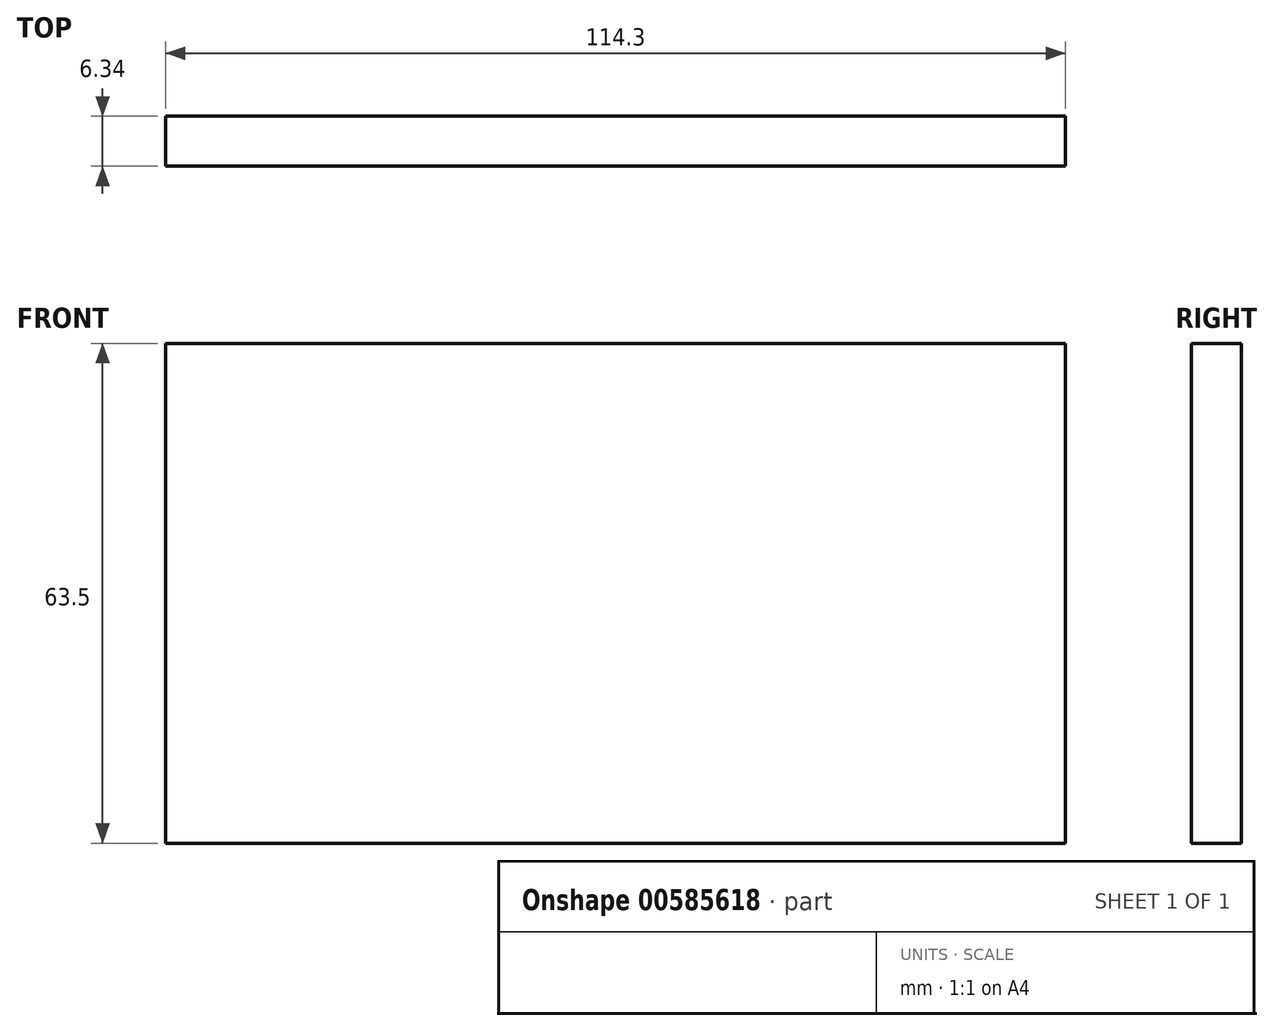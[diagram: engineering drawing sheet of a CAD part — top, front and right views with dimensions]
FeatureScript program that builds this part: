
annotation { "Feature Type Name" : "Feature", "Feature Type Description" : "" }
export const myFeature = defineFeature(function(context is Context, id is Id, definition is map)
    precondition{}
    {
        {
            var Q0;
            Q0=qCreatedBy(makeId("Top.planeOp"),FACE);
            var sketch = newSketch(context, id + "F0", { "sketchPlane" : qUnion([Q0])});
            skLineSegment(sketch, "E0.bottom", {"start": v(-57.15, 3.17) * mm, "end": v(57.15, 3.18) * mm});
            skLineSegment(sketch, "E0.top", {"start": v(-57.15, -3.18) * mm, "end": v(57.15, -3.17) * mm});
            skLineSegment(sketch, "E0.left", {"start": v(-57.15, 3.17) * mm, "end": v(-57.15, -3.18) * mm});
            skLineSegment(sketch, "E0.right", {"start": v(57.15, 3.18) * mm, "end": v(57.15, -3.17) * mm});
            skPoint(sketch, "E0.middle", {"position": v(0, 0) * mm});
            skSolve(sketch);
        }
        {
            var Q0;
            Q0=makeQuery(id+"F0.imprint","IMPRINT",FACE,{"disambiguationData":[TD([[makeQuery(id+"F0.imprint","IMPRINT",EDGE,{"derivedFrom":sQuery(id+"F0.wireOp",EDGE,"E0.bottom")}),-1.0]])]});
            extrude(context, id + "F1", {"entities" : qUnion([Q0]), "depth" : 63.5 * mm, "offsetDistance" : 25.4 * mm});
        }
    });
